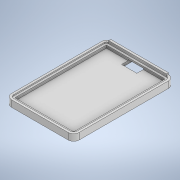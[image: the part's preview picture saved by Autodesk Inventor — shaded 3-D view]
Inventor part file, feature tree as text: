
AUTODESK INVENTOR PART (.ipt)
format: ipt  version: 2022 (Build 260153000, 153)  size: 192,000 bytes
history: native  units: in
note: dims shown in document units (in); Inventor stores cm internally (conversion verified against a paired STEP export)
features: extrude x5, sketch x5
ambient origin geometry x8: Origin, YZ Plane, XZ Plane, XY Plane, X Axis, Y Axis, Z Axis, Center Point
bodies: Solid1 (feature_tree)
feature tree (10):
  extrude  "Extrusion1"  Depth=3.4646in
  extrude  "Extrusion2"  Depth=0.1181in
  extrude  "Extrusion3"  Depth=0.0394in TaperAngle=0.0deg
  extrude  "Extrusion4"  Depth=0.0591in
  extrude  "Extrusion5"  Depth=0.1575in
  sketch  "Sketch1"  dims[d0=2.2835in d1=3.4646in]
  sketch  "Sketch2"  dims[d2=0.0787in d3=0.1181in]
  sketch  "Sketch3"  dims[d4=0.0787in d5=0.0394in d6=0.0in]
  sketch  "Sketch4"  dims[d7=0.0984in d8=0.0in d9=0.0591in]
  sketch  "Sketch5"  dims[d10=0.0787in d11=0.0in d12=0.1575in d13=0.0984in d14=0.0in d16=0.5512in d17=0.0in d18=0.1378in d19=0.3937in d20=0.0in]
